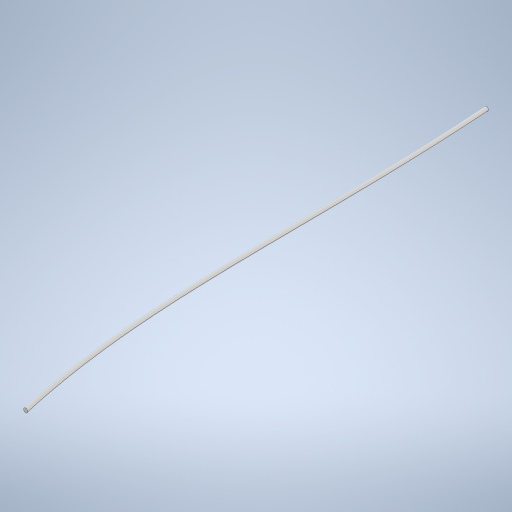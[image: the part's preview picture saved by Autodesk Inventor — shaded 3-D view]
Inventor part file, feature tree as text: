
AUTODESK INVENTOR PART (.ipt)
format: ipt  version: 2024.2 (Build 282272000, 272)  size: 248,832 bytes
history: native  units: in
note: dims shown in document units (in); Inventor stores cm internally (conversion verified against a paired STEP export)
features: sketch x2, sweep x1
ambient origin geometry x8: Origin, YZ Plane, XZ Plane, XY Plane, X Axis, Y Axis, Z Axis, Center Point
bodies: Solid1 (feature_tree)
feature tree (3):
  sweep  "Sweep1"
  sketch  "Sketch1"  dims[d0=0.012in d1=0.0in d2=0.0in]
  sketch  "Sketch2"
